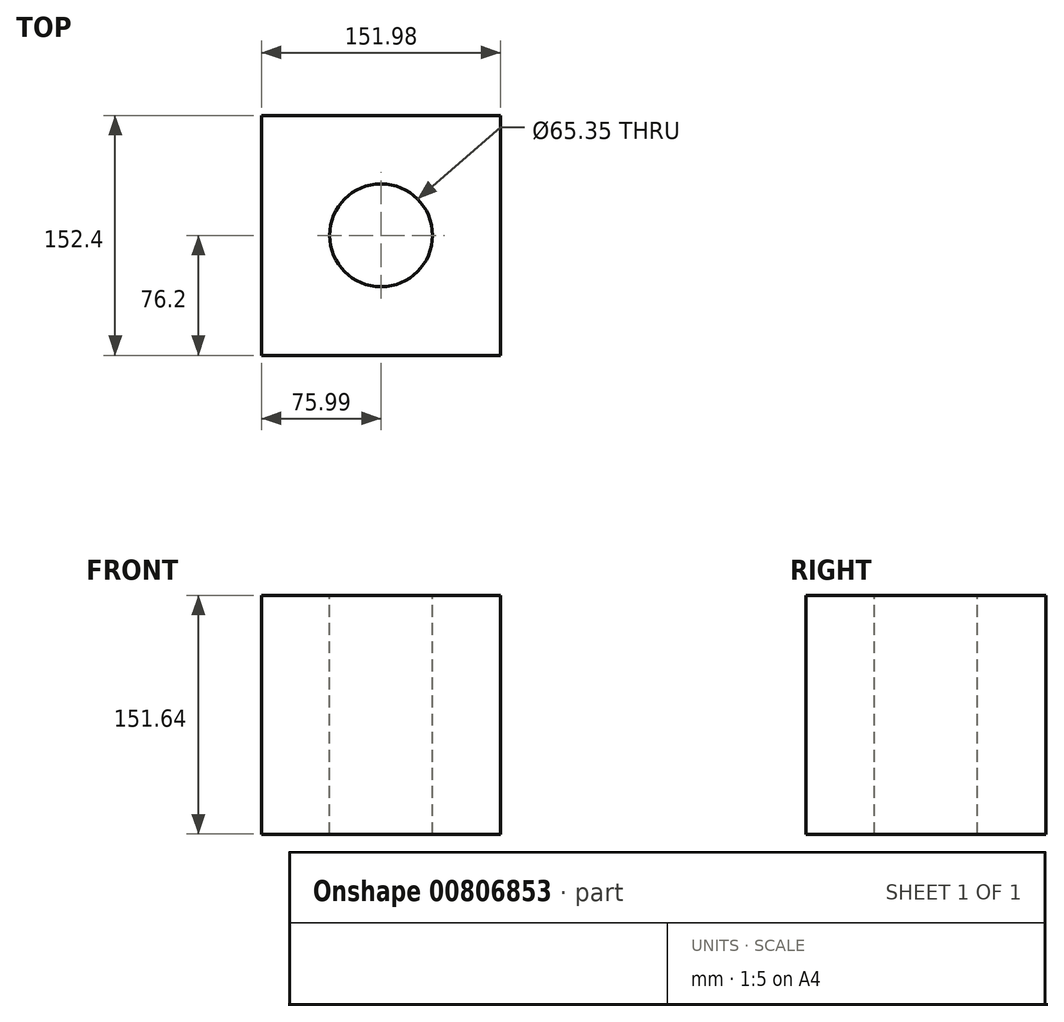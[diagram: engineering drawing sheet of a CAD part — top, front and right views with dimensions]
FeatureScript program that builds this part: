
annotation { "Feature Type Name" : "Feature", "Feature Type Description" : "" }
export const myFeature = defineFeature(function(context is Context, id is Id, definition is map)
    precondition{}
    {
        {
            var Q0;
            Q0=qCreatedBy(makeId("Front.planeOp"),FACE);
            var sketch = newSketch(context, id + "F0", { "sketchPlane" : qUnion([Q0])});
            skLineSegment(sketch, "E0.bottom", {"start": v(-76, 75.82) * mm, "end": v(76, 75.82) * mm});
            skLineSegment(sketch, "E0.top", {"start": v(-76, -75.82) * mm, "end": v(76, -75.82) * mm});
            skLineSegment(sketch, "E0.left", {"start": v(-76, 75.82) * mm, "end": v(-76, -75.82) * mm});
            skLineSegment(sketch, "E0.right", {"start": v(76, 75.82) * mm, "end": v(76, -75.82) * mm});
            skPoint(sketch, "E0.middle", {"position": v(0, 0) * mm});
            skSolve(sketch);
        }
        {
            var Q0;
            Q0 = qSketchRegion(id + "F0", true);
            extrude(context, id + "F1", {"entities" : qUnion([Q0]), "endBound" : BoundingType.SYMMETRIC, "depth" : 152.4 * mm, "offsetDistance" : 25.4 * mm});
        }
        {
            var Q0;
            Q0=makeQuery(id+"F1.opExtrude","SWEPT_FACE",FACE,{"disambiguationData":[OSD([sQuery(id+"F0.wireOp",EDGE,"E0.bottom")])]});
            var sketch = newSketch(context, id + "F2", { "sketchPlane" : qUnion([Q0])});
            skCircle(sketch, "E1", {"center": v(0, 0) * mm, "radius": 32.67 * mm});
            skSolve(sketch);
        }
        {
            var Q0;
            Q0=makeQuery(id+"F2.imprint","IMPRINT",FACE,{"disambiguationData":[TD([[makeQuery(id+"F2.imprint","IMPRINT",EDGE,{"derivedFrom":sQuery(id+"F2.wireOp",EDGE,"E1")}),1.0]])]});
            extrude(context, id + "F3", {"entities" : qUnion([Q0]), "operationType" : NewBodyOperationType.REMOVE, "endBound" : BoundingType.THROUGH_ALL, "oppositeDirection" : true, "depth" : 25.4 * mm, "offsetDistance" : 25.4 * mm});
        }
    });
